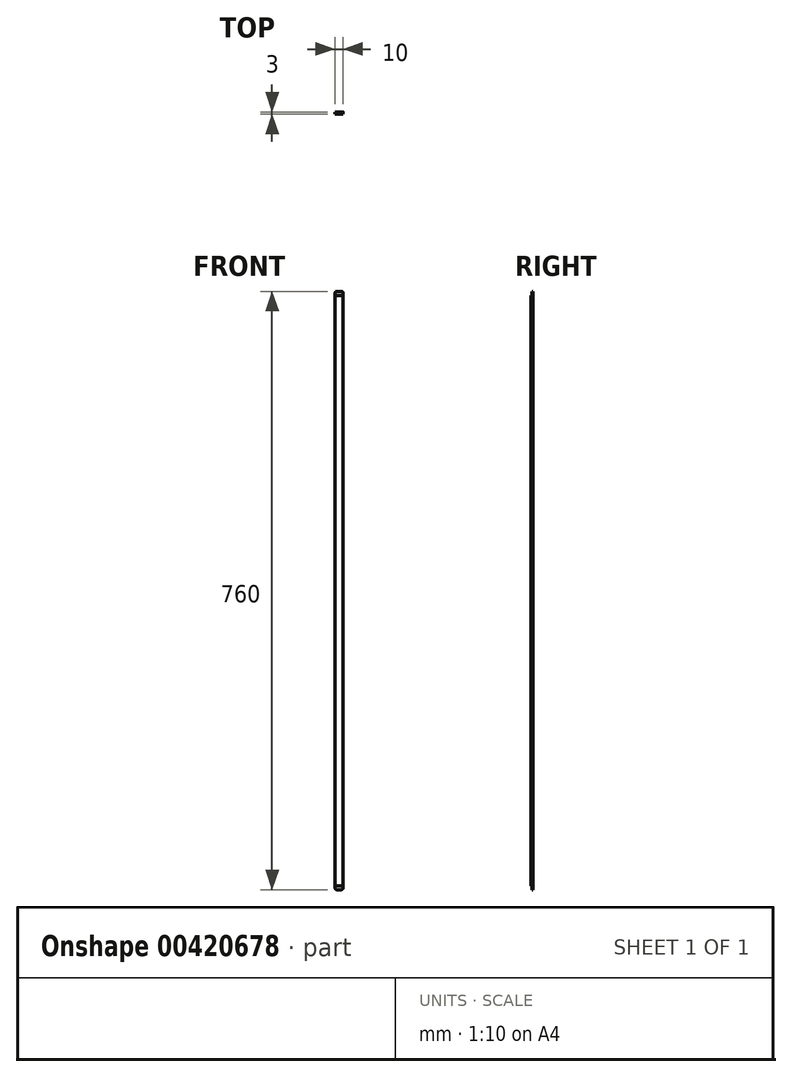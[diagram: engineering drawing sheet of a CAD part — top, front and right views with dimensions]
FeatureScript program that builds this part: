
annotation { "Feature Type Name" : "Feature", "Feature Type Description" : "" }
export const myFeature = defineFeature(function(context is Context, id is Id, definition is map)
    precondition{}
    {
        {
            var Q0;
            Q0=qCreatedBy(makeId("Front.planeOp"),FACE);
            var sketch = newSketch(context, id + "F0", { "sketchPlane" : qUnion([Q0])});
            skLineSegment(sketch, "E0.bottom", {"start": v(5, -380) * mm, "end": v(-5, -380) * mm});
            skLineSegment(sketch, "E0.top", {"start": v(5, 380) * mm, "end": v(-5, 380) * mm});
            skLineSegment(sketch, "E0.left", {"start": v(5, -380) * mm, "end": v(5, 380) * mm});
            skLineSegment(sketch, "E0.right", {"start": v(-5, -380) * mm, "end": v(-5, 380) * mm});
            skPoint(sketch, "E0.middle", {"position": v(0, 0) * mm});
            skSolve(sketch);
        }
        {
            var Q0;
            Q0=qSketchRegion(id+"F0",true);
            extrude(context, id + "F1", {"entities" : qUnion([Q0]), "depth" : 3 * mm});
        }
        {
            var Q0;
            Q0=makeQuery(id+"F1.opExtrude","CAP_FACE",FACE,{"disambiguationData":[OSD([sQuery(id+"F0.wireOp",EDGE,"E0.bottom"),sQuery(id+"F0.wireOp",EDGE,"E0.top"),sQuery(id+"F0.wireOp",EDGE,"E0.left"),sQuery(id+"F0.wireOp",EDGE,"E0.right")])],"isStart":false});
            var sketch = newSketch(context, id + "F2", { "sketchPlane" : qUnion([Q0])});
            skLineSegment(sketch, "E1", {"start": v(-5, 380) * mm, "end": v(5, 380) * mm});
            skLineSegment(sketch, "E2", {"start": v(5, 380) * mm, "end": v(5, 375) * mm});
            skLineSegment(sketch, "E3", {"start": v(5, 375) * mm, "end": v(-5, 375) * mm});
            skLineSegment(sketch, "E4", {"start": v(-5, 375) * mm, "end": v(-5, 380) * mm});
            skLineSegment(sketch, "E5", {"start": v(5, -380) * mm, "end": v(5, -375) * mm});
            skLineSegment(sketch, "E6", {"start": v(5, -375) * mm, "end": v(-5, -375) * mm});
            skLineSegment(sketch, "E7", {"start": v(-5, -375) * mm, "end": v(-5, -380) * mm});
            skSolve(sketch);
        }
        {
            var Q0;
            Q0=qSketchRegion(id+"F2",true);
            var Q1;
            Q1=makeQuery(id+"F2.imprint","IMPRINT",FACE,{"disambiguationData":[TD([[makeQuery(id+"F2.imprint","IMPRINT",EDGE,{"derivedFrom":sQuery(id+"F2.wireOp",EDGE,"E5")}),1.0]])]});
            extrude(context, id + "F3", {"entities" : qUnion([Q0, Q1]), "operationType" : NewBodyOperationType.REMOVE, "oppositeDirection" : true, "depth" : 1.5 * mm});
        }
        {
            var Q0;
            Q0=makeQuery(id+"F1.opExtrude","SWEPT_EDGE",EDGE,{"disambiguationData":[OSD([sQuery(id+"F0.wireOp",EDGE,"E0.bottom"),sQuery(id+"F0.wireOp",EDGE,"E0.left")])]});
            var Q1;
            Q1=makeQuery(id+"F1.opExtrude","SWEPT_EDGE",EDGE,{"disambiguationData":[OSD([sQuery(id+"F0.wireOp",EDGE,"E0.bottom"),sQuery(id+"F0.wireOp",EDGE,"E0.right")])]});
            var Q2;
            Q2=makeQuery(id+"F1.opExtrude","SWEPT_EDGE",EDGE,{"disambiguationData":[OSD([sQuery(id+"F0.wireOp",EDGE,"E0.top"),sQuery(id+"F0.wireOp",EDGE,"E0.right")])]});
            var Q3;
            Q3=makeQuery(id+"F1.opExtrude","SWEPT_EDGE",EDGE,{"disambiguationData":[OSD([sQuery(id+"F0.wireOp",EDGE,"E0.top"),sQuery(id+"F0.wireOp",EDGE,"E0.left")])]});
            fillet(context, id + "F4", {"entities" : qUnion([Q0, Q1, Q2, Q3]), "radius" : 2 * mm, "tangentPropagation" : true, "allowEdgeOverflow" : false});
        }
    });
